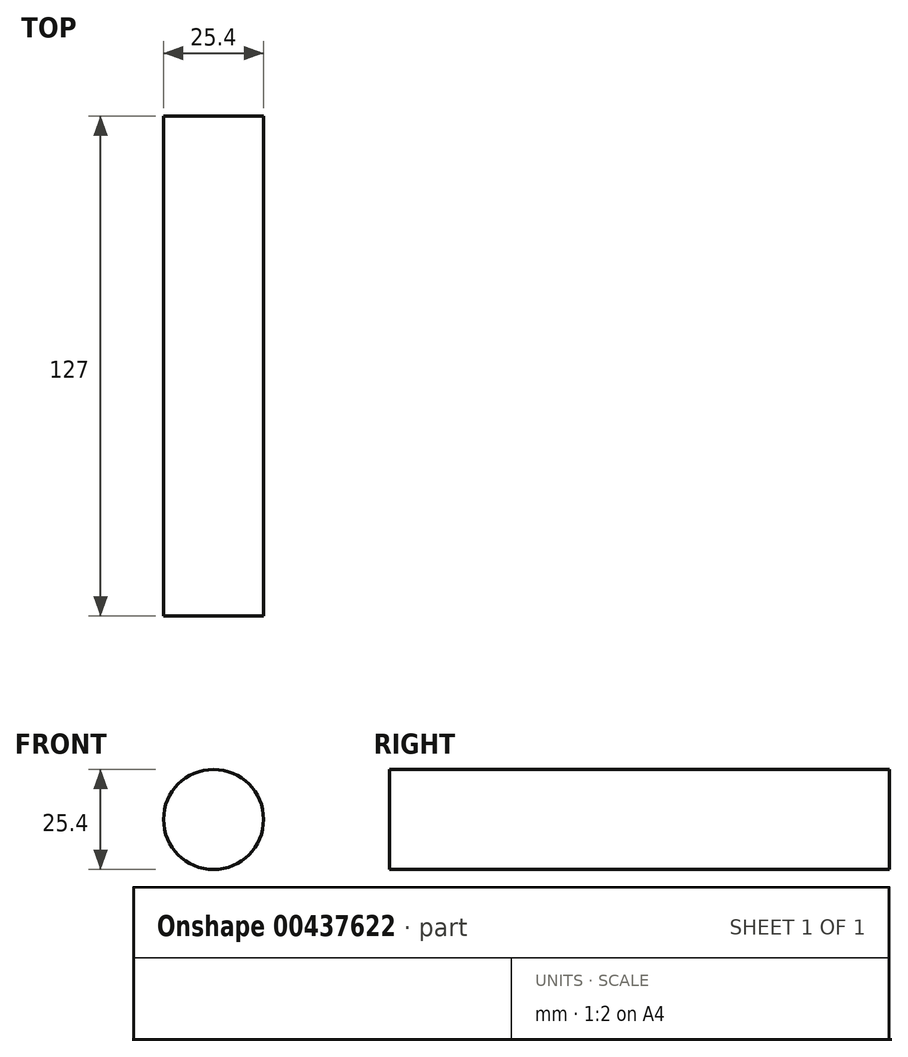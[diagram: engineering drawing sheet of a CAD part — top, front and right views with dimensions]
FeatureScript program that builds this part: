
annotation { "Feature Type Name" : "Feature", "Feature Type Description" : "" }
export const myFeature = defineFeature(function(context is Context, id is Id, definition is map)
    precondition{}
    {
        {
            var Q0;
            Q0=qCreatedBy(makeId("Front.planeOp"),FACE);
            var sketch = newSketch(context, id + "F0", { "sketchPlane" : qUnion([Q0])});
            skCircle(sketch, "E0", {"center": v(0, 0) * mm, "radius": 12.7 * mm});
            skSolve(sketch);
        }
        {
            var Q0;
            Q0=qSketchRegion(id+"F0",true);
            extrude(context, id + "F1", {"entities" : qUnion([Q0]), "depth" : 127 * mm});
        }
    });
